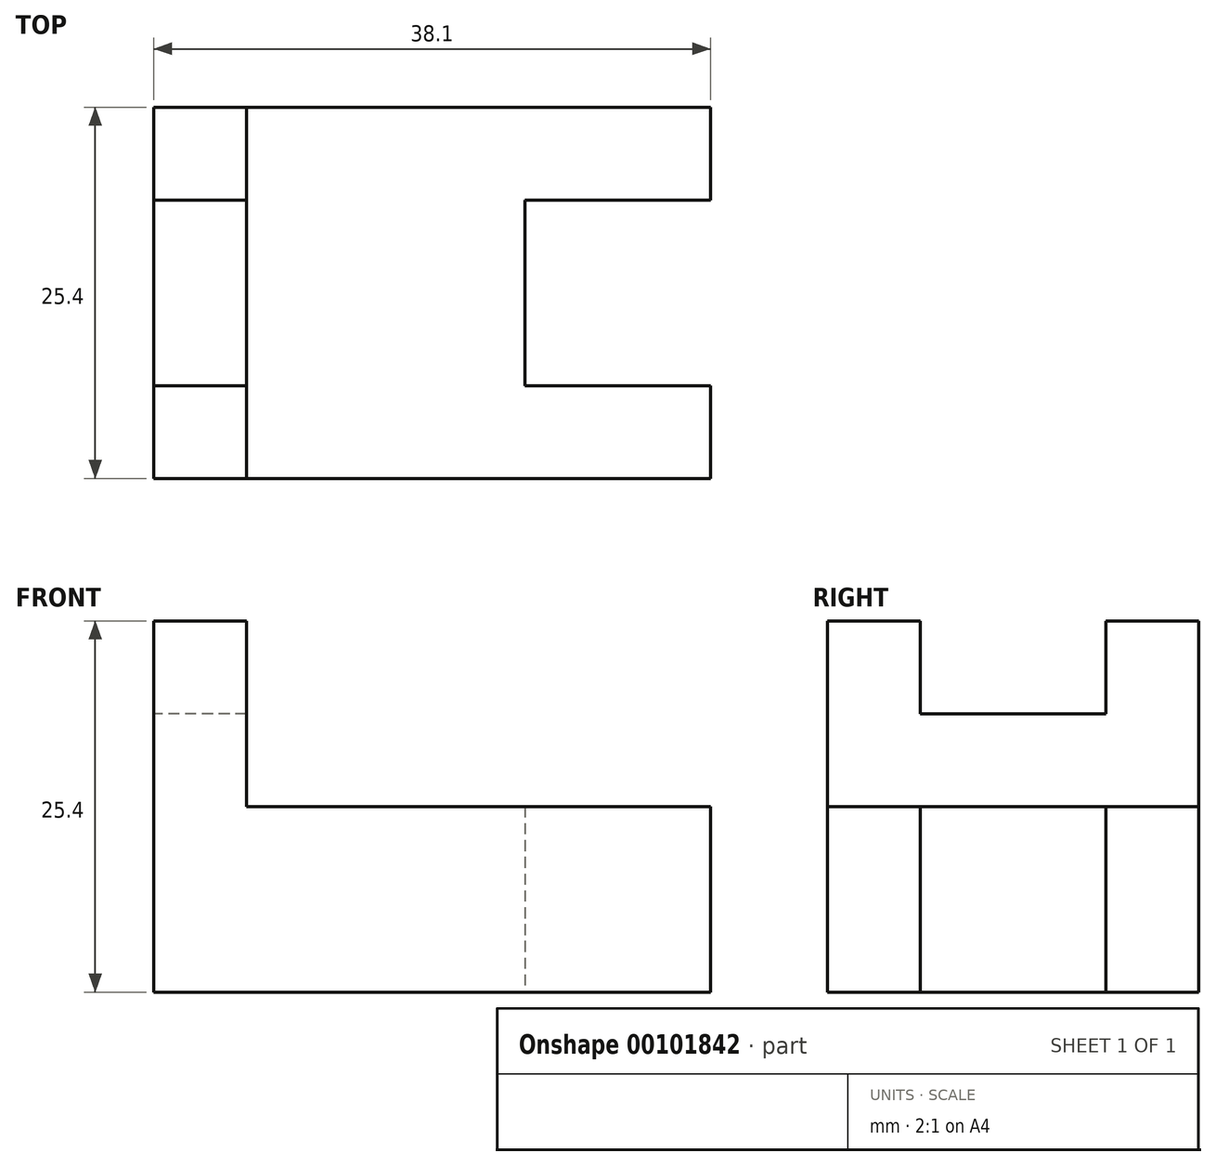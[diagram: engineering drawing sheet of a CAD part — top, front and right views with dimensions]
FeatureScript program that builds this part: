
annotation { "Feature Type Name" : "Feature", "Feature Type Description" : "" }
export const myFeature = defineFeature(function(context is Context, id is Id, definition is map)
    precondition{}
    {
        {
            var Q0;
            Q0=qCreatedBy(makeId("Top.planeOp"),FACE);
            var sketch = newSketch(context, id + "F0", { "sketchPlane" : qUnion([Q0])});
            skLineSegment(sketch, "E0", {"start": v(0, 0) * mm, "end": v(38.1, 0) * mm});
            skLineSegment(sketch, "E1", {"start": v(38.1, 0) * mm, "end": v(38.1, 6.35) * mm});
            skLineSegment(sketch, "E2", {"start": v(38.1, 6.35) * mm, "end": v(25.4, 6.35) * mm});
            skLineSegment(sketch, "E3", {"start": v(25.4, 6.35) * mm, "end": v(25.4, 19.05) * mm});
            skLineSegment(sketch, "E4", {"start": v(25.4, 19.05) * mm, "end": v(38.1, 19.05) * mm});
            skLineSegment(sketch, "E5", {"start": v(38.1, 19.05) * mm, "end": v(38.1, 25.4) * mm});
            skLineSegment(sketch, "E6", {"start": v(38.1, 25.4) * mm, "end": v(0, 25.4) * mm});
            skLineSegment(sketch, "E7", {"start": v(0, 25.4) * mm, "end": v(0, 0) * mm});
            skSolve(sketch);
        }
        {
            var Q0;
            Q0 = qSketchRegion(id + "F0", true);
            extrude(context, id + "F1", {"entities" : qUnion([Q0]), "depth" : 12.7 * mm});
        }
        {
            var Q0;
            Q0=makeQuery(id+"F1.opExtrude","SWEPT_FACE",FACE,{"disambiguationData":[OSD([sQuery(id+"F0.wireOp",EDGE,"E7")])]});
            var sketch = newSketch(context, id + "F2", { "sketchPlane" : qUnion([Q0])});
            skLineSegment(sketch, "E8", {"start": v(-25.4, 12.7) * mm, "end": v(-25.4, 25.4) * mm});
            skLineSegment(sketch, "E9", {"start": v(-25.4, 25.4) * mm, "end": v(-19.05, 25.4) * mm});
            skLineSegment(sketch, "E10", {"start": v(-19.05, 25.4) * mm, "end": v(-19.05, 19.05) * mm});
            skLineSegment(sketch, "E11", {"start": v(-19.05, 19.05) * mm, "end": v(-6.35, 19.05) * mm});
            skLineSegment(sketch, "E12", {"start": v(-6.35, 19.05) * mm, "end": v(-6.35, 25.4) * mm});
            skLineSegment(sketch, "E13", {"start": v(-6.35, 25.4) * mm, "end": v(0, 25.4) * mm});
            skLineSegment(sketch, "E14", {"start": v(0, 25.4) * mm, "end": v(0, 12.7) * mm});
            skSolve(sketch);
        }
        {
            var Q0;
            Q0=makeQuery(id+"F2.imprint","IMPRINT",FACE,{"disambiguationData":[TD([[makeQuery(id+"F2.imprint","IMPRINT",EDGE,{"derivedFrom":sQuery(id+"F2.wireOp",EDGE,"E8")}),-1.0]])]});
            extrude(context, id + "F3", {"entities" : qUnion([Q0]), "operationType" : NewBodyOperationType.ADD, "oppositeDirection" : true, "depth" : 6.35 * mm});
        }
    });
